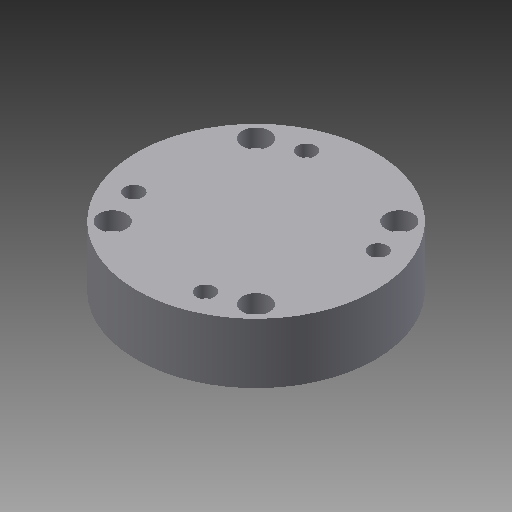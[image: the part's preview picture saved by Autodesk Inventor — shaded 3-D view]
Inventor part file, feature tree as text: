
AUTODESK INVENTOR PART (.ipt)
format: ipt  version: 2019.4 (Build 234330000, 330)  size: 271,360 bytes
history: native  units: in
note: dims shown in document units (in); Inventor stores cm internally (conversion verified against a paired STEP export)
features: other x273, sketch x9, hole x6, revolve x3, thread x1, pattern_linear x1
ambient origin geometry x8: Origin, YZ Plane, XZ Plane, XY Plane, X Axis, Y Axis, Z Axis, Center Point
bodies: Solid1 (feature_tree)
feature tree (293):
  revolve  "Revolution1"  Angle=360.0deg
  revolve  "Revolution2"  Angle=360.0deg
  thread  "Thread1"  [1 undecoded]
  revolve  "Revolution3"  [1 undecoded]
  hole  "Hole1"  [1 undecoded]
  hole  "Hole2"  [1 undecoded]
  hole  "Hole3"  [1 undecoded]
  hole  "Hole4"  [1 undecoded]
  hole  "Hole5"  [1 undecoded]
  hole  "Hole6"  [1 undecoded]
  pattern_linear  "Rectangular Pattern1"  [2 undecoded]
  other  "a1_XY"
  other  "a1_YZ"
  other  "a1_ZX"
  other  "a1_X"
  other  "a1_Y"
  other  "a1_Z"
  other  "a1_Center"
  other  "a2_XY"
  other  "a2_YZ"
  other  "a2_ZX"
  other  "a2_X"
  other  "a2_Y"
  other  "a2_Z"
  other  "a2_Center"
  other  "ar3_XY"
  other  "ar3_YZ"
  other  "ar3_ZX"
  other  "ar3_X"
  other  "ar3_Y"
  other  "ar3_Z"
  other  "ar3_Center"
  other  "ar4_XY"
  other  "ar4_YZ"
  other  "ar4_ZX"
  other  "ar4_X"
  other  "ar4_Y"
  other  "ar4_Z"
  other  "ar4_Center"
  other  "ar5_XY"
  other  "ar5_YZ"
  other  "ar5_ZX"
  other  "ar5_X"
  other  "ar5_Y"
  other  "ar5_Z"
  other  "ar5_Center"
  other  "ar6_XY"
  other  "ar6_YZ"
  other  "ar6_ZX"
  other  "ar6_X"
  other  "ar6_Y"
  other  "ar6_Z"
  other  "ar6_Center"
  other  "b1_XY"
  other  "b1_YZ"
  other  "b1_ZX"
  other  "b1_X"
  other  "b1_Y"
  other  "b1_Z"
  other  "b1_Center"
  other  "c11_XY"
  other  "c11_YZ"
  other  "c11_ZX"
  other  "c11_X"
  other  "c11_Y"
  other  "c11_Z"
  other  "c11_Center"
  other  "c22_XY"
  other  "c22_YZ"
  other  "c22_ZX"
  other  "c22_X"
  other  "c22_Y"
  other  "c22_Z"
  other  "c22_Center"
  other  "d11_XY"
  other  "d11_YZ"
  other  "d11_ZX"
  other  "d11_X"
  other  "d11_Y"
  other  "d11_Z"
  other  "d11_Center"
  other  "d22_XY"
  other  "d22_YZ"
  other  "d22_ZX"
  other  "d22_X"
  other  "d22_Y"
  other  "d22_Z"
  other  "d22_Center"
  other  "j_XY"
  other  "j_YZ"
  other  "j_ZX"
  other  "j_X"
  other  "j_Y"
  other  "j_Z"
  other  "j_Center"
  other  "k1_XY"
  other  "k1_YZ"
  other  "k1_ZX"
  other  "k1_X"
  other  "k1_Y"
  other  "k1_Z"
  other  "k1_Center"
  other  "k2_XY"
  other  "k2_YZ"
  other  "k2_ZX"
  other  "k2_X"
  other  "k2_Y"
  other  "k2_Z"
  other  "k2_Center"
  other  "po1_XY"
  other  "po1_YZ"
  other  "po1_ZX"
  other  "po1_X"
  other  "po1_Y"
  other  "po1_Z"
  other  "po1_Center"
  other  "po2_XY"
  other  "po2_YZ"
  other  "po2_ZX"
  other  "po2_X"
  other  "po2_Y"
  other  "po2_Z"
  other  "po2_Center"
  other  "po3_XY"
  other  "po3_YZ"
  other  "po3_ZX"
  other  "po3_X"
  other  "po3_Y"
  other  "po3_Z"
  other  "po3_Center"
  other  "r7_XY"
  other  "r7_YZ"
  other  "r7_ZX"
  other  "r7_X"
  other  "r7_Y"
  other  "r7_Z"
  other  "r7_Center"
  other  "r71_XY"
  other  "r71_YZ"
  other  "r71_ZX"
  other  "r71_X"
  other  "r71_Y"
  other  "r71_Z"
  other  "r71_Center"
  other  "r72_XY"
  other  "r72_YZ"
  other  "r72_ZX"
  other  "r72_X"
  other  "r72_Y"
  other  "r72_Z"
  other  "r72_Center"
  other  "r73_XY"
  other  "r73_YZ"
  other  "r73_ZX"
  other  "r73_X"
  other  "r73_Y"
  other  "r73_Z"
  other  "r73_Center"
  other  "rg_XY"
  other  "rg_YZ"
  other  "rg_ZX"
  other  "rg_X"
  other  "rg_Y"
  other  "rg_Z"
  other  "rg_Center"
  other  "rh_XY"
  other  "rh_YZ"
  other  "rh_ZX"
  other  "rh_X"
  other  "rh_Y"
  other  "rh_Z"
  other  "rh_Center"
  other  "rs_1_XY"
  other  "rs_1_YZ"
  other  "rs_1_ZX"
  other  "rs_1_X"
  other  "rs_1_Y"
  other  "rs_1_Z"
  other  "rs_1_Center"
  other  "rs_2_XY"
  other  "rs_2_YZ"
  other  "rs_2_ZX"
  other  "rs_2_X"
  other  "rs_2_Y"
  other  "rs_2_Z"
  other  "rs_2_Center"
  other  "rs_3_XY"
  other  "rs_3_YZ"
  other  "rs_3_ZX"
  other  "rs_3_X"
  other  "rs_3_Y"
  other  "rs_3_Z"
  other  "rs_3_Center"
  other  "rs_4_XY"
  other  "rs_4_YZ"
  other  "rs_4_ZX"
  other  "rs_4_X"
  other  "rs_4_Y"
  other  "rs_4_Z"
  other  "rs_4_Center"
  other  "sc1_XY"
  other  "sc1_YZ"
  other  "sc1_ZX"
  other  "sc1_X"
  other  "sc1_Y"
  other  "sc1_Z"
  other  "sc1_Center"
  other  "sc2_XY"
  other  "sc2_YZ"
  other  "sc2_ZX"
  other  "sc2_X"
  other  "sc2_Y"
  other  "sc2_Z"
  other  "sc2_Center"
  other  "sc3_XY"
  other  "sc3_YZ"
  other  "sc3_ZX"
  other  "sc3_X"
  other  "sc3_Y"
  other  "sc3_Z"
  other  "sc3_Center"
  other  "to_dummy_XY"
  other  "to_dummy_YZ"
  other  "to_dummy_ZX"
  other  "to_dummy_X"
  other  "to_dummy_Y"
  other  "to_dummy_Z"
  other  "to_dummy_Center"
  other  "to_nut_XY"
  other  "to_nut_YZ"
  other  "to_nut_ZX"
  other  "to_nut_X"
  other  "to_nut_Y"
  other  "to_nut_Z"
  other  "to_nut_Center"
  other  "to_rod_XY"
  other  "to_rod_YZ"
  other  "to_rod_ZX"
  other  "to_rod_X"
  other  "to_rod_Y"
  other  "to_rod_Z"
  other  "to_rod_Center"
  other  "to_tube_XY"
  other  "to_tube_YZ"
  other  "to_tube_ZX"
  other  "to_tube_X"
  other  "to_tube_Y"
  other  "to_tube_Z"
  other  "to_tube_Center"
  other  "to_wiper_XY"
  other  "to_wiper_YZ"
  other  "to_wiper_ZX"
  other  "to_wiper_X"
  other  "to_wiper_Y"
  other  "to_wiper_Z"
  other  "to_wiper_Center"
  other  "track1_XY"
  other  "track1_YZ"
  other  "track1_ZX"
  other  "track1_X"
  other  "track1_Y"
  other  "track1_Z"
  other  "track1_Center"
  other  "track2_XY"
  other  "track2_YZ"
  other  "track2_ZX"
  other  "track2_X"
  other  "track2_Y"
  other  "track2_Z"
  other  "track2_Center"
  other  "track3_XY"
  other  "track3_YZ"
  other  "track3_ZX"
  other  "track3_X"
  other  "track3_Y"
  other  "track3_Z"
  other  "track3_Center"
  other  "track4_XY"
  other  "track4_YZ"
  other  "track4_ZX"
  other  "track4_X"
  other  "track4_Y"
  other  "track4_Z"
  other  "track4_Center"
  sketch  "Sketch_1"  dims[d0=360.0deg d1=360.0deg]
  sketch  "Sketch_84"  dims[d40=0.104in d41=0.5in d42=0.15in d43=0.1in d44=0.5635in d45=0.5in d46=0.0in d47=0.7874in d49=1.1003in d50=0.7874in d52=1.1003in]
  sketch  "Sketch_85"  dims[d53=0.0in d54=0.0in d55=0.0in d56=0.0in d57=0.0in d58=0.0in d59=0.0in d60=0.0in d61=0.0in d62=0.0in d63=0.0in d64=0.0in d65=0.0in d66=0.0in d67=0.0in d68=0.0in d69=0.0in d70=0.0in d71=0.0in d72=0.0in d73=0.0in d74=0.0in d75=0.0in d76=0.0in d77=0.0in]
  sketch  "Sketch4"  dims[d2=0.3302in d3=0.0in d4=360.0deg]
  sketch  "Sketch5"  dims[d5=0.156in d6=0.75in d7=0.226in d8=0.148in d9=0.5635in d10=0.5in d11=0.0in]
  sketch  "Sketch6"  dims[d12=0.156in d13=0.75in d14=0.226in d15=0.148in d16=0.5635in d17=0.5in d18=0.0in]
  sketch  "Sketch7"  dims[d19=0.156in d20=0.75in d21=0.226in d22=0.148in d23=0.5635in d24=0.5in d25=0.0in]
  sketch  "Sketch8"  dims[d26=0.156in d27=0.75in d28=0.226in d29=0.148in d30=0.5635in d31=0.5in d32=0.0in]
  sketch  "Sketch9"  dims[d33=1.122in d34=0.75in d35=0.375in d36=0.25in d37=0.5635in d38=0.218in d39=0.0in]
note: 10 required parameter values undecoded (feature->parameter linkage not recoverable at this tier; creation-order binding heuristic only, values carry confidence <= 0.55)
